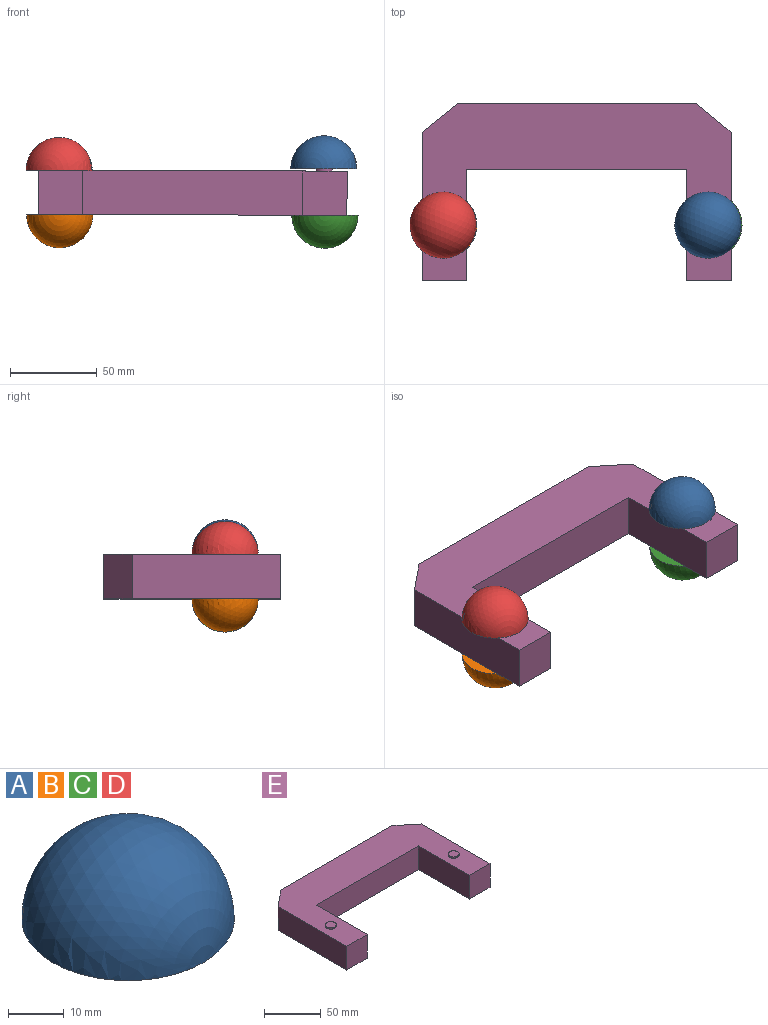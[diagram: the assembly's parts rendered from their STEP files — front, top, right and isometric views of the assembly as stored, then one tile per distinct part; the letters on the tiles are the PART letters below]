
ASSEMBLY  parts=5 mates=4
PART A: 2 faces, bbox 38.1x38.1x19.1 mm
  f0: sphere r=19.05mm, area 2280.2mm2, adj f1
  f1: plane 38.1x38.1mm, normal (0,0,-1), area 1140.1mm2, adj f0
PART B: same geometry as A
PART C: same geometry as A
PART D: same geometry as A
PART E: 20 faces, bbox 177.8x101.6x27.9 mm
  f0: plane 63.5x25.4mm, normal (1,0,0), area 1612.9mm2, adj f1,f7,f8,f9
  f1: plane 127x25.4mm, normal (0,-1,0), area 3225.8mm2, adj f0,f2,f8,f9
  f2: plane 63.5x25.4mm, normal (-1,0,0), area 1612.9mm2, adj f1,f3,f8,f9
  f3: plane 25.4x25.4mm, normal (0,-1,0), area 645.2mm2, adj f2,f4,f8,f9
  f4: plane 85.2x25.4mm, normal (1,0,0), area 2164.2mm2, adj f3,f8,f9,f11
  f5: plane 137.55x25.4mm, normal (0,1,0), area 3493.8mm2, adj f8,f9,f10,f11
  f6: plane 85.25x25.4mm, normal (-1,0,0), area 2165.4mm2, adj f7,f8,f9,f10
  f7: plane 25.4x25.4mm, normal (0,-1,0), area 645.2mm2, adj f0,f6,f8,f9
  f8: plane 177.8x101.6mm, normal (0,0,1), area 9528mm2, adj f0,f1,f2,f3,f4,f5,f6,f7
  f9: plane 177.8x101.6mm, normal (0,0,-1), area 9528mm2, adj f0,f1,f2,f3,f4,f5,f6,f7
  f10: plane 25.4x20.17mm, normal (-0.63,0.78,0), area 659.5mm2, adj f5,f6,f8,f9
  f11: plane 25.4x20.08mm, normal (0.63,0.77,0), area 658.4mm2, adj f4,f5,f8,f9
  f12: cylinder r=4.76mm len=9.53mm, axis (0,0,-1), area 38mm2, adj f8,f13
  f13: plane 9.53x9.53mm, normal (0,0,1), area 71.3mm2, adj f12
  f14: cylinder r=4.76mm len=9.53mm, axis (0,0,-1), area 38mm2, adj f8,f15
  f15: plane 9.53x9.53mm, normal (0,0,1), area 71.3mm2, adj f14
  f16: cylinder r=4.76mm len=9.53mm, axis (0,0,1), area 38mm2, adj f9,f17
  f17: plane 9.53x9.53mm, normal (0,0,-1), area 71.3mm2, adj f16
  f18: cylinder r=4.76mm len=9.53mm, axis (0,0,1), area 38mm2, adj f9,f19
  f19: plane 9.53x9.53mm, normal (0,0,-1), area 71.3mm2, adj f18
PLACE A rot(axis=(0,0,-1),22.5deg) t=(-38.09,90.85,40.86)mm
PLACE B rot(axis=(0,-1,0),179.9deg) t=(-190.13,90.85,14.48)mm
PLACE C rot(axis=(0,-1,0),179.9deg) t=(-37.51,90.85,14.18)mm
PLACE D rot(axis=(0,0,-1),22.5deg) t=(-190.5,90.85,39.88)mm
PLACE E rot(axis=(0,1,0),0.1deg) t=(-120.04,108.02,14.35)mm
MATE revolute E.f12 <-> D.f1  axis (0,0,1) through (-190.5,90.85,39.88)mm
MATE revolute E.f14 <-> A.f1  axis (0,0,1) through (-38.09,90.85,40.86)mm
MATE revolute E.f16 <-> B.f1  axis (0,0,-1) through (-190.13,90.85,14.48)mm
MATE revolute E.f18 <-> C.f1  axis (0,0,-1) through (-37.51,90.85,14.18)mm
